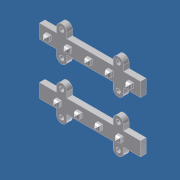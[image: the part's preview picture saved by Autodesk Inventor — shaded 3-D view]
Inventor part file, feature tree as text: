
AUTODESK INVENTOR PART (.ipt)
format: ipt  version: unknown  size: 422,912 bytes
history: native  units: in
note: dims shown in document units (in); Inventor stores cm internally (conversion verified against a paired STEP export)
features: extrude x4, sketch x4, chamfer x1, fillet x1
ambient origin geometry x8: Origin, YZ Plane, XZ Plane, XY Plane, X Axis, Y Axis, Z Axis, Center Point
feature tree (10):
  extrude  "Extrusion2"  Depth=0.2in TaperAngle=0.0deg
  extrude  "Extrusion3"  Depth=0.085in TaperAngle=45.0deg
  extrude  "Extrusion4"  Depth=0.2in TaperAngle=0.0deg
  chamfer  "Chamfer1"  [1 undecoded]
  fillet  "Fillet1"  [1 undecoded]
  extrude  "Extrusion7"  [1 undecoded]
  sketch  "Sketch1"  dims[d14=0.2in d15=0.0in d16=0.2in d17=0.0in]
  sketch  "Sketch2"  dims[d18=0.2in d19=0.0in d20=0.085in d21=0.125in d22=45.0deg]
  sketch  "Sketch3"  dims[d23=0.125in d36=0.2in d37=0.0in]
  sketch  "Sketch4"
note: 3 required parameter values undecoded (feature->parameter linkage not recoverable at this tier; creation-order binding heuristic only, values carry confidence <= 0.55)
